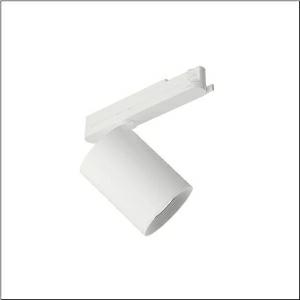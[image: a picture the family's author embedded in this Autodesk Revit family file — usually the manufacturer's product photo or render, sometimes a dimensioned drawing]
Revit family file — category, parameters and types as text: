
# Revit family: spot_21_51se14mbb5b
name_source: partatom
category: Lighting Fixtures
units: mm (PartAtom-declared; Revit-internal decimal feet)

## family parameters
Cut with Voids When Loaded = No
Host = Face
Light Source = No
Part Type = Normal
Room Calculation Point = No
Round Connector Dimension = Use Diameter
Shared = No

## types (1)
- --- (1 x LED, 5530 lm, 41.8 W, 3000K)
    Apparent Load = 42 VA
    CIE Flux Codes = 96 99 100 100 100
    Color Rendering = 90
    Color Temperature = 3000K
    Default Elevation = 1800 mm
    Description = Spot 21, directional spotlight, light control with lens, of PMMA, LED rated luminous flux: 5.110lm, light colour: 930, control gear: ECG Multilumen, with 3-phase adapter, mains connection: 220..240V, AC, 50/60Hz, of aluminium, traffic white (RAL 9016), length: 213mm, diameter: 105mm, protection rating (complete): IP20, insulation class (complete): insulation class I (protective earthing), certification: CE, impact resistance: IK02, permissible ambient temperature for indoor applications: -20..+40°C, packaging unit: 1 piece
    Height = 175 mm
    Lamp = 1 x LED
    Lamp Light Flux = 5530 lm
    Lamp Power = 41.8 W
    Lamp count = 1
    Length = 105 mm
    Luminous efficacy = 132 lm/W
    Manufacturer = Siteco
    ModVariant = No
    Model = 51SE14MBB5B
    Mounting Place = Ceiling
    Mounting Type = Pendant
    Number of Poles = 1
    OnlyDefault = Yes
    Power Factor = 1
    Product Name = Spot 21
    Product group = directional spotlight
    ProductGroupID = 904
    Protection Class = Protection class I
    Protection Degree = IP 20
    RLX_Detail_Level = 1
    RlxData = <blob elided: 17637 chars, md5=ec67bef5>
    Socket = socket
    Standby Power = 0 W
    System Light Flux = 5530 lm
    System Power = 42 W
    Type Comments = factory setting: luminous flux: 100 % | (ON | ON | ON | ON) | 1050 mA
    Type Image = l_1003976.jpg
    URL = http://relux.com
    VarID = @adj_052829
    Voltage = 0 V
    Weight = 0.00 kg
    Width = 0 mm  [stored 0 ft]

note: [stored X ft] marks values corroborated as IEEE doubles in the binary element streams (Revit-internal decimal feet)

## geometry (parser evidence)
native form markers: Blend x4, Sweep x9
no freeform markers — native parametric forms only
